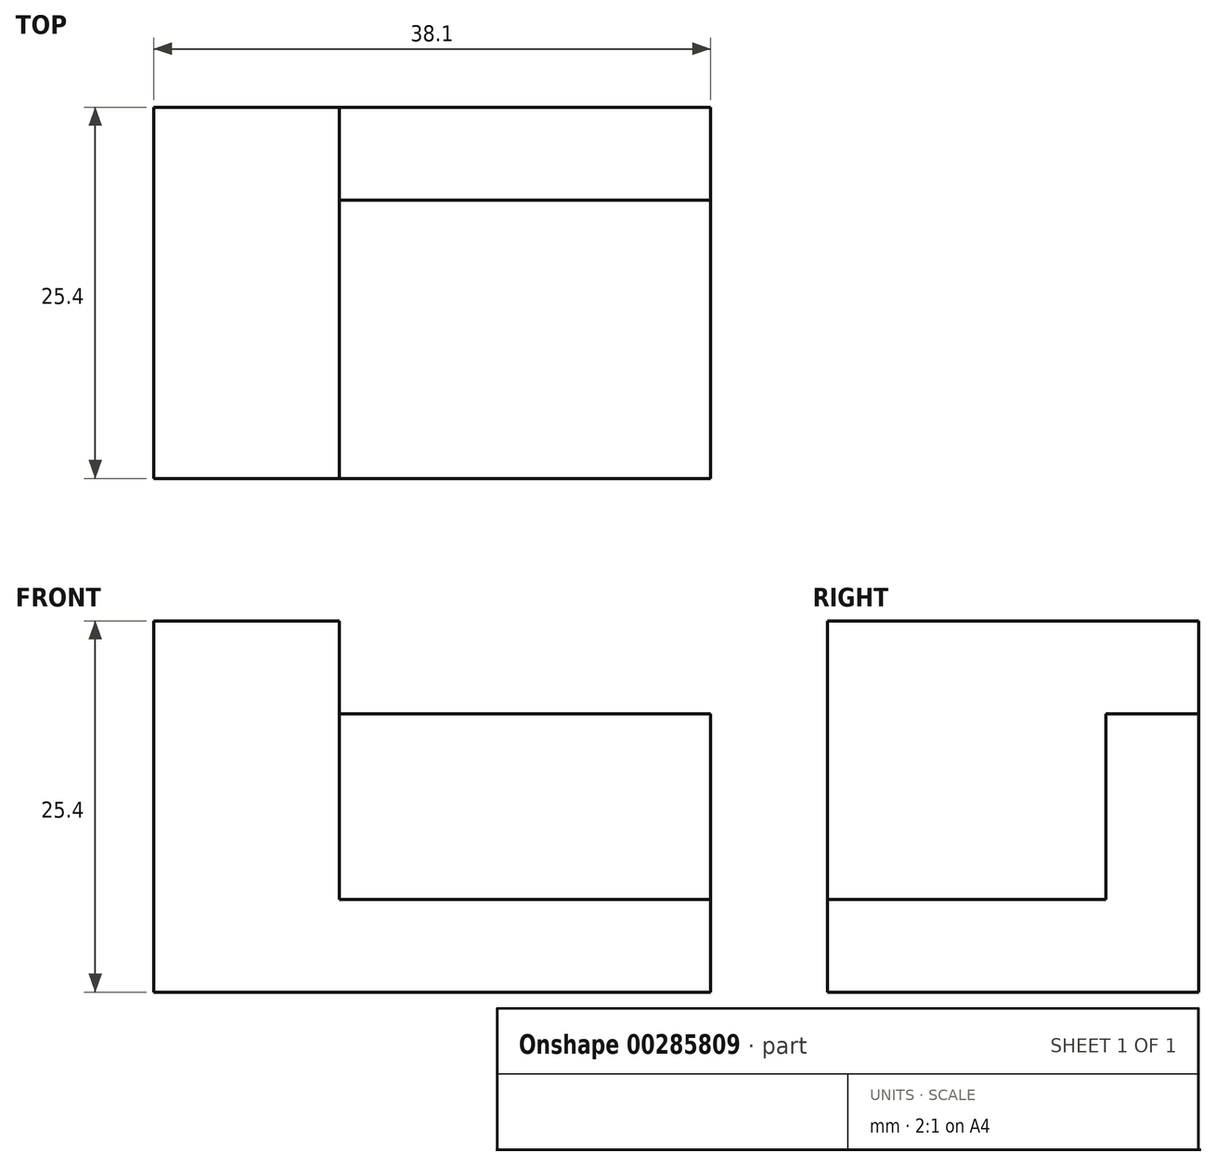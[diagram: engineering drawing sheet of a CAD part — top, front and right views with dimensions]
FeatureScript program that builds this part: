
annotation { "Feature Type Name" : "Feature", "Feature Type Description" : "" }
export const myFeature = defineFeature(function(context is Context, id is Id, definition is map)
    precondition{}
    {
        {
            var Q0;
            Q0=qCreatedBy(makeId("Front.planeOp"),FACE);
            var sketch = newSketch(context, id + "F0", { "sketchPlane" : qUnion([Q0])});
            skLineSegment(sketch, "E0", {"start": v(0, 0) * mm, "end": v(0, 25.4) * mm});
            skLineSegment(sketch, "E1", {"start": v(0, 25.4) * mm, "end": v(12.7, 25.4) * mm});
            skLineSegment(sketch, "E2", {"start": v(12.7, 25.4) * mm, "end": v(12.7, 6.35) * mm});
            skLineSegment(sketch, "E3", {"start": v(12.7, 6.35) * mm, "end": v(38.1, 6.35) * mm});
            skLineSegment(sketch, "E4", {"start": v(38.1, 6.35) * mm, "end": v(38.1, 0) * mm});
            skLineSegment(sketch, "E5", {"start": v(38.1, 0) * mm, "end": v(0, 0) * mm});
            skSolve(sketch);
        }
        {
            var Q0;
            Q0=makeQuery(id+"F0.imprint","IMPRINT",FACE,{"disambiguationData":[TD([[makeQuery(id+"F0.imprint","IMPRINT",EDGE,{"derivedFrom":sQuery(id+"F0.wireOp",EDGE,"E0")}),-1.0]])]});
            extrude(context, id + "F1", {"entities" : qUnion([Q0]), "depth" : 25.4 * mm, "symmetric" : true});
        }
        {
            var Q0;
            Q0=makeQuery(id+"F1.opExtrude","CAP_FACE",FACE,{"disambiguationData":[OSD([sQuery(id+"F0.wireOp",EDGE,"E0"),sQuery(id+"F0.wireOp",EDGE,"E1"),sQuery(id+"F0.wireOp",EDGE,"E2"),sQuery(id+"F0.wireOp",EDGE,"E3"),sQuery(id+"F0.wireOp",EDGE,"E4"),sQuery(id+"F0.wireOp",EDGE,"E5")])],"isStart":true});
            var sketch = newSketch(context, id + "F2", { "sketchPlane" : qUnion([Q0])});
            skLineSegment(sketch, "E6", {"start": v(-12.7, 19.05) * mm, "end": v(-38.1, 19.05) * mm});
            skLineSegment(sketch, "E7", {"start": v(-38.1, 19.05) * mm, "end": v(-38.1, 6.35) * mm});
            skSolve(sketch);
        }
        {
            var Q0;
            {var subQ0=sQuery(id+"F2.wireOp",EDGE,"E6");Q0=makeQuery(id+"F2.imprint","IMPRINT",FACE,{"disambiguationData":[TD([[makeQuery(id+"F2.imprint","IMPRINT",EDGE,{"derivedFrom":subQ0}),1.0]])]});}
            extrude(context, id + "F3", {"entities" : qUnion([Q0]), "operationType" : NewBodyOperationType.ADD, "oppositeDirection" : true, "depth" : 6.35 * mm});
        }
    });
